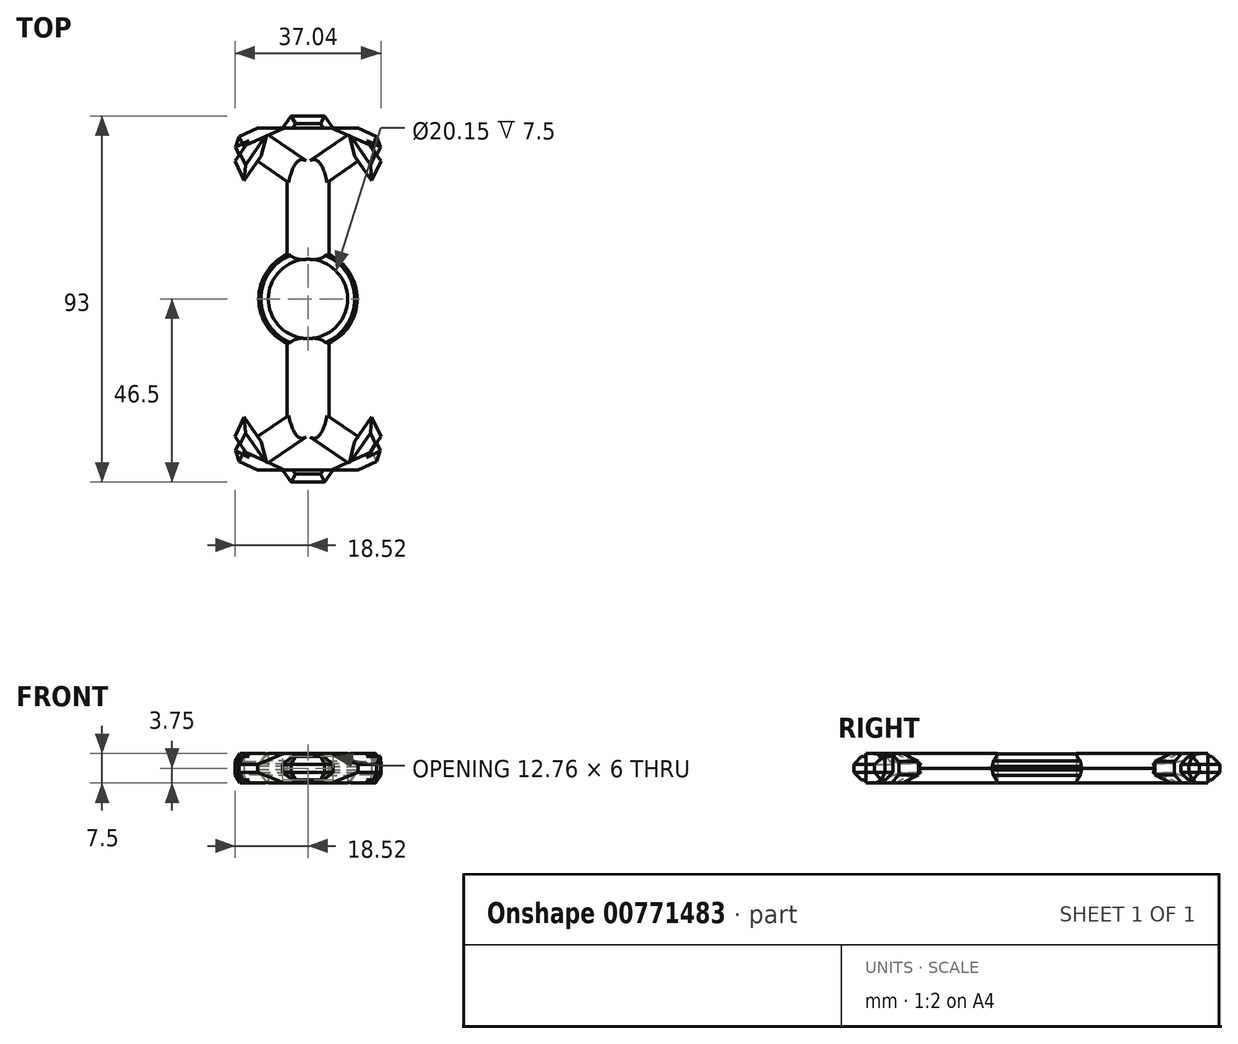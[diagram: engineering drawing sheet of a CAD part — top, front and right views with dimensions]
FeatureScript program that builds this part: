
annotation { "Feature Type Name" : "Feature", "Feature Type Description" : "" }
export const myFeature = defineFeature(function(context is Context, id is Id, definition is map)
    precondition{}
    {
        {
            var Q0;
            Q0=qCreatedBy(makeId("Top.planeOp"),FACE);
            var sketch = newSketch(context, id + "F0", { "sketchPlane" : qUnion([Q0])});
            skCircle(sketch, "E0", {"center": v(0, 0) * mm, "radius": 12.5 * mm});
            skLineSegment(sketch, "E1", {"start": v(0, 0) * mm, "end": v(5.5, 0) * mm});
            skLineSegment(sketch, "E2", {"start": v(5.5, 0) * mm, "end": v(-5.5, 0) * mm});
            skLineSegment(sketch, "E3", {"start": v(-5.5, 0) * mm, "end": v(-5.5, -35) * mm});
            skLineSegment(sketch, "E4", {"start": v(-5.5, -35) * mm, "end": v(5.5, -35) * mm});
            skLineSegment(sketch, "E5", {"start": v(5.5, -35) * mm, "end": v(5.5, 0) * mm});
            skLineSegment(sketch, "E6.MirrorCS", {"start": v(-5.5, 0) * mm, "end": v(-5.5, 35) * mm});
            skLineSegment(sketch, "E7.MirrorCS", {"start": v(-5.5, 35) * mm, "end": v(5.5, 35) * mm});
            skLineSegment(sketch, "E8.MirrorCS", {"start": v(5.5, 35) * mm, "end": v(5.5, 0) * mm});
            skLineSegment(sketch, "E9", {"start": v(5.5, -30.02) * mm, "end": v(12.76, -35) * mm});
            skLineSegment(sketch, "E10", {"start": v(12.76, -35) * mm, "end": v(16.17, -30.02) * mm});
            skLineSegment(sketch, "E11", {"start": v(16.17, -30.02) * mm, "end": v(18.52, -35) * mm});
            skLineSegment(sketch, "E12", {"start": v(18.52, -35) * mm, "end": v(12.76, -43.4) * mm});
            skLineSegment(sketch, "E13", {"start": v(12.76, -43.4) * mm, "end": v(0, -43.4) * mm});
            skLineSegment(sketch, "E14.MirrorCS", {"start": v(-5.5, -30.02) * mm, "end": v(-12.76, -35) * mm});
            skLineSegment(sketch, "E15.MirrorCS", {"start": v(-12.76, -35) * mm, "end": v(-16.17, -30.02) * mm});
            skLineSegment(sketch, "E16.MirrorCS", {"start": v(-16.17, -30.02) * mm, "end": v(-18.52, -35) * mm});
            skLineSegment(sketch, "E17.MirrorCS", {"start": v(-18.52, -35) * mm, "end": v(-12.76, -43.4) * mm});
            skLineSegment(sketch, "E18.MirrorCS", {"start": v(-12.76, -43.4) * mm, "end": v(0, -43.4) * mm});
            skLineSegment(sketch, "E19", {"start": v(-17.43, -36.6) * mm, "end": v(-19.38, -40.43) * mm});
            skLineSegment(sketch, "E20", {"start": v(-19.38, -40.43) * mm, "end": v(-12.76, -43.4) * mm});
            skLineSegment(sketch, "E21.MirrorCS", {"start": v(19.38, -40.43) * mm, "end": v(12.76, -43.4) * mm});
            skLineSegment(sketch, "E22.MirrorCS", {"start": v(17.43, -36.6) * mm, "end": v(19.38, -40.43) * mm});
            skLineSegment(sketch, "E23.MirrorCS", {"start": v(12.76, 43.4) * mm, "end": v(0, 43.4) * mm});
            skLineSegment(sketch, "E24.MirrorCS", {"start": v(-12.76, 43.4) * mm, "end": v(0, 43.4) * mm});
            skLineSegment(sketch, "E25.MirrorCS", {"start": v(-19.38, 40.43) * mm, "end": v(-12.76, 43.4) * mm});
            skLineSegment(sketch, "E26.MirrorCS", {"start": v(-17.43, 36.6) * mm, "end": v(-19.38, 40.43) * mm});
            skLineSegment(sketch, "E27.MirrorCS", {"start": v(-16.17, 30.02) * mm, "end": v(-18.52, 35) * mm});
            skLineSegment(sketch, "E28.MirrorCS", {"start": v(-18.52, 35) * mm, "end": v(-12.76, 43.4) * mm});
            skLineSegment(sketch, "E29.MirrorCS", {"start": v(-12.76, 35) * mm, "end": v(-16.17, 30.02) * mm});
            skLineSegment(sketch, "E30.MirrorCS", {"start": v(-5.5, 30.02) * mm, "end": v(-12.76, 35) * mm});
            skLineSegment(sketch, "E31.MirrorCS", {"start": v(5.5, 30.02) * mm, "end": v(12.76, 35) * mm});
            skLineSegment(sketch, "E32.MirrorCS", {"start": v(12.76, 35) * mm, "end": v(16.17, 30.02) * mm});
            skLineSegment(sketch, "E33.MirrorCS", {"start": v(18.52, 35) * mm, "end": v(12.76, 43.4) * mm});
            skLineSegment(sketch, "E34.MirrorCS", {"start": v(16.17, 30.02) * mm, "end": v(18.52, 35) * mm});
            skLineSegment(sketch, "E35.MirrorCS", {"start": v(19.38, 40.43) * mm, "end": v(12.76, 43.4) * mm});
            skLineSegment(sketch, "E36.MirrorCS", {"start": v(17.43, 36.6) * mm, "end": v(19.38, 40.43) * mm});
            skLineSegment(sketch, "E37", {"start": v(-6.38, -43.4) * mm, "end": v(-4.25, -46.5) * mm});
            skLineSegment(sketch, "E38", {"start": v(-4.25, -46.5) * mm, "end": v(0, -46.5) * mm});
            skLineSegment(sketch, "E39.MirrorCS", {"start": v(4.25, -46.5) * mm, "end": v(0, -46.5) * mm});
            skLineSegment(sketch, "E40.MirrorCS", {"start": v(6.38, -43.4) * mm, "end": v(4.25, -46.5) * mm});
            skLineSegment(sketch, "E41.MirrorCS", {"start": v(-6.38, 43.4) * mm, "end": v(-4.25, 46.5) * mm});
            skLineSegment(sketch, "E42.MirrorCS", {"start": v(4.25, 46.5) * mm, "end": v(0, 46.5) * mm});
            skLineSegment(sketch, "E43.MirrorCS", {"start": v(-4.25, 46.5) * mm, "end": v(0, 46.5) * mm});
            skLineSegment(sketch, "E44.MirrorCS", {"start": v(6.38, 43.4) * mm, "end": v(4.25, 46.5) * mm});
            skCircle(sketch, "E45", {"center": v(0, 0) * mm, "radius": 10.07 * mm});
            skSolve(sketch);
        }
        {
            var Q0;
            {var subQ0=sQuery(id+"F0.wireOp",EDGE,"E6.MirrorCS");var subQ1=sQuery(id+"F0.wireOp",EDGE,"E0");var subQ2=makeQuery(id+"F0.imprint","INTERSECT",VERTEX,{"derivedFrom":[subQ1,subQ0]});Q0=makeQuery(id+"F0.imprint","IMPRINT",FACE,{"disambiguationData":[TD([[makeQuery(id+"F0.imprint","IMPRINT",EDGE,{"disambiguationData":[TD([[subQ2,-1.0]])],"derivedFrom":subQ1}),1.0]])]});}
            var Q1;
            {var subQ0=sQuery(id+"F0.wireOp",EDGE,"E8.MirrorCS");var subQ1=sQuery(id+"F0.wireOp",EDGE,"E0");var subQ2=makeQuery(id+"F0.imprint","INTERSECT",VERTEX,{"derivedFrom":[subQ1,subQ0]});Q1=makeQuery(id+"F0.imprint","IMPRINT",FACE,{"disambiguationData":[TD([[makeQuery(id+"F0.imprint","IMPRINT",EDGE,{"disambiguationData":[TD([[subQ2,1.0]])],"derivedFrom":subQ1}),1.0]])]});}
            var Q2;
            {var subQ0=sQuery(id+"F0.wireOp",EDGE,"E3");var subQ3=sQuery(id+"F0.wireOp",EDGE,"E0");var subQ4=makeQuery(id+"F0.imprint","INTERSECT",VERTEX,{"derivedFrom":[subQ3,subQ0]});Q2=makeQuery(id+"F0.imprint","IMPRINT",FACE,{"disambiguationData":[TD([[makeQuery(id+"F0.imprint","IMPRINT",EDGE,{"disambiguationData":[TD([[subQ4,-1.0]])],"derivedFrom":subQ3}),1.0]])]});}
            var Q3;
            {var subQ0=sQuery(id+"F0.wireOp",EDGE,"E6.MirrorCS");var subQ3=sQuery(id+"F0.wireOp",EDGE,"E0");var subQ4=makeQuery(id+"F0.imprint","INTERSECT",VERTEX,{"derivedFrom":[subQ3,subQ0]});Q3=makeQuery(id+"F0.imprint","IMPRINT",FACE,{"disambiguationData":[TD([[makeQuery(id+"F0.imprint","IMPRINT",EDGE,{"disambiguationData":[TD([[subQ4,1.0]])],"derivedFrom":subQ3}),1.0]])]});}
            var Q4;
            {var subQ9=sQuery(id+"F0.wireOp",EDGE,"E7.MirrorCS");Q4=makeQuery(id+"F0.imprint","IMPRINT",FACE,{"disambiguationData":[TD([[makeQuery(id+"F0.imprint","IMPRINT",EDGE,{"derivedFrom":subQ9}),1.0]])]});}
            var Q5;
            {var subQ8=sQuery(id+"F0.wireOp",EDGE,"E4");Q5=makeQuery(id+"F0.imprint","IMPRINT",FACE,{"disambiguationData":[TD([[makeQuery(id+"F0.imprint","IMPRINT",EDGE,{"derivedFrom":subQ8}),-1.0]])]});}
            var Q6;
            {var subQ0=sQuery(id+"F0.wireOp",EDGE,"E4");Q6=makeQuery(id+"F0.imprint","IMPRINT",FACE,{"disambiguationData":[TD([[makeQuery(id+"F0.imprint","IMPRINT",EDGE,{"derivedFrom":subQ0}),1.0]])]});}
            var Q7;
            {var subQ0=sQuery(id+"F0.wireOp",EDGE,"E7.MirrorCS");Q7=makeQuery(id+"F0.imprint","IMPRINT",FACE,{"disambiguationData":[TD([[makeQuery(id+"F0.imprint","IMPRINT",EDGE,{"derivedFrom":subQ0}),-1.0]])]});}
            extrude(context, id + "F1", {"entities" : qUnion([Q0, Q1, Q2, Q3, Q4, Q5, Q6, Q7]), "endBound" : BoundingType.SYMMETRIC, "depth" : 7.5 * mm, "offsetDistance" : 25 * mm});
        }
        {
            var Q0;
            {var subQ0=sQuery(id+"F0.wireOp",EDGE,"E0");Q0=makeQuery(id+"F1.opExtrude","CAP_EDGE",EDGE,{"disambiguationData":[OSD([subQ0]),TDD([makeQuery(id+"F0.imprint","IMPRINT",EDGE,{"disambiguationData":[TD([[makeQuery(id+"F0.imprint","INTERSECT",VERTEX,{"derivedFrom":[subQ0,sQuery(id+"F0.wireOp",EDGE,"E6.MirrorCS")]}),-1.0]])],"derivedFrom":subQ0})])],"isStart":false});}
            var Q1;
            {var subQ0=sQuery(id+"F0.wireOp",EDGE,"E0");Q1=makeQuery(id+"F1.opExtrude","CAP_EDGE",EDGE,{"disambiguationData":[OSD([subQ0]),TDD([makeQuery(id+"F0.imprint","IMPRINT",EDGE,{"disambiguationData":[TD([[makeQuery(id+"F0.imprint","INTERSECT",VERTEX,{"derivedFrom":[subQ0,sQuery(id+"F0.wireOp",EDGE,"E8.MirrorCS")]}),1.0]])],"derivedFrom":subQ0})])],"isStart":false});}
            var Q2;
            {var subQ0=sQuery(id+"F0.wireOp",EDGE,"E0");Q2=makeQuery(id+"F1.opExtrude","CAP_EDGE",EDGE,{"disambiguationData":[OSD([subQ0]),TDD([makeQuery(id+"F0.imprint","IMPRINT",EDGE,{"disambiguationData":[TD([[makeQuery(id+"F0.imprint","INTERSECT",VERTEX,{"derivedFrom":[subQ0,sQuery(id+"F0.wireOp",EDGE,"E6.MirrorCS")]}),-1.0]])],"derivedFrom":subQ0})])],"isStart":true});}
            var Q3;
            {var subQ0=sQuery(id+"F0.wireOp",EDGE,"E0");Q3=makeQuery(id+"F1.opExtrude","CAP_EDGE",EDGE,{"disambiguationData":[OSD([subQ0]),TDD([makeQuery(id+"F0.imprint","IMPRINT",EDGE,{"disambiguationData":[TD([[makeQuery(id+"F0.imprint","INTERSECT",VERTEX,{"derivedFrom":[subQ0,sQuery(id+"F0.wireOp",EDGE,"E8.MirrorCS")]}),1.0]])],"derivedFrom":subQ0})])],"isStart":true});}
            chamfer(context, id + "F2", {"entities" : qUnion([Q0, Q1, Q2, Q3]), "width" : 2.5 * mm, "tangentPropagation" : true});
        }
        {
            var Q0;
            Q0=makeQuery(id+"F1.opExtrude","CAP_EDGE",EDGE,{"disambiguationData":[OSD([sQuery(id+"F0.wireOp",EDGE,"E5")])],"isStart":false});
            var Q1;
            Q1=makeQuery(id+"F1.opExtrude","CAP_EDGE",EDGE,{"disambiguationData":[OSD([sQuery(id+"F0.wireOp",EDGE,"E3")])],"isStart":false});
            var Q2;
            Q2=makeQuery(id+"F1.opExtrude","CAP_EDGE",EDGE,{"disambiguationData":[OSD([sQuery(id+"F0.wireOp",EDGE,"E3")])],"isStart":true});
            var Q3;
            Q3=makeQuery(id+"F1.opExtrude","CAP_EDGE",EDGE,{"disambiguationData":[OSD([sQuery(id+"F0.wireOp",EDGE,"E5")])],"isStart":true});
            var Q4;
            Q4=makeQuery(id+"F1.opExtrude","CAP_EDGE",EDGE,{"disambiguationData":[OSD([sQuery(id+"F0.wireOp",EDGE,"E6.MirrorCS")])],"isStart":true});
            var Q5;
            Q5=makeQuery(id+"F1.opExtrude","CAP_EDGE",EDGE,{"disambiguationData":[OSD([sQuery(id+"F0.wireOp",EDGE,"E6.MirrorCS")])],"isStart":false});
            var Q6;
            Q6=makeQuery(id+"F1.opExtrude","CAP_EDGE",EDGE,{"disambiguationData":[OSD([sQuery(id+"F0.wireOp",EDGE,"E8.MirrorCS")])],"isStart":true});
            var Q7;
            Q7=makeQuery(id+"F1.opExtrude","CAP_EDGE",EDGE,{"disambiguationData":[OSD([sQuery(id+"F0.wireOp",EDGE,"E8.MirrorCS")])],"isStart":false});
            fillet(context, id + "F3", {"entities" : qUnion([Q0, Q1, Q2, Q3, Q4, Q5, Q6, Q7]), "radius" : 5 * mm, "tangentPropagation" : true, "allowEdgeOverflow" : false});
        }
        {
            var Q0;
            {var subQ3=sQuery(id+"F0.wireOp",EDGE,"E37");Q0=makeQuery(id+"F0.imprint","IMPRINT",FACE,{"disambiguationData":[TD([[makeQuery(id+"F0.imprint","IMPRINT",EDGE,{"derivedFrom":subQ3}),1.0]])]});}
            var Q1;
            {var subQ0=sQuery(id+"F0.wireOp",EDGE,"E21.MirrorCS");Q1=makeQuery(id+"F0.imprint","IMPRINT",FACE,{"disambiguationData":[TD([[makeQuery(id+"F0.imprint","IMPRINT",EDGE,{"derivedFrom":subQ0}),-1.0]])]});}
            var Q2;
            {var subQ2=sQuery(id+"F0.wireOp",EDGE,"E19");Q2=makeQuery(id+"F0.imprint","IMPRINT",FACE,{"disambiguationData":[TD([[makeQuery(id+"F0.imprint","IMPRINT",EDGE,{"derivedFrom":subQ2}),1.0]])]});}
            var Q3;
            {var subQ0=sQuery(id+"F0.wireOp",EDGE,"E25.MirrorCS");Q3=makeQuery(id+"F0.imprint","IMPRINT",FACE,{"disambiguationData":[TD([[makeQuery(id+"F0.imprint","IMPRINT",EDGE,{"derivedFrom":subQ0}),-1.0]])]});}
            var Q4;
            {var subQ0=sQuery(id+"F0.wireOp",EDGE,"E41.MirrorCS");Q4=makeQuery(id+"F0.imprint","IMPRINT",FACE,{"disambiguationData":[TD([[makeQuery(id+"F0.imprint","IMPRINT",EDGE,{"derivedFrom":subQ0}),-1.0]])]});}
            var Q5;
            {var subQ0=sQuery(id+"F0.wireOp",EDGE,"E35.MirrorCS");Q5=makeQuery(id+"F0.imprint","IMPRINT",FACE,{"disambiguationData":[TD([[makeQuery(id+"F0.imprint","IMPRINT",EDGE,{"derivedFrom":subQ0}),1.0]])]});}
            extrude(context, id + "F4", {"entities" : qUnion([Q0, Q1, Q2, Q3, Q4, Q5]), "operationType" : NewBodyOperationType.ADD, "endBound" : BoundingType.SYMMETRIC, "depth" : 6 * mm, "offsetDistance" : 25 * mm});
        }
        {
            var Q0;
            Q0=makeQuery(id+"F4.opExtrude","CAP_EDGE",EDGE,{"disambiguationData":[OSD([sQuery(id+"F0.wireOp",EDGE,"E42.MirrorCS"),sQuery(id+"F0.wireOp",EDGE,"E43.MirrorCS")])],"isStart":false});
            var Q1;
            Q1=makeQuery(id+"F4.opExtrude","CAP_EDGE",EDGE,{"disambiguationData":[OSD([sQuery(id+"F0.wireOp",EDGE,"E42.MirrorCS"),sQuery(id+"F0.wireOp",EDGE,"E43.MirrorCS")])],"isStart":true});
            var Q2;
            Q2=makeQuery(id+"F4.opExtrude","CAP_EDGE",EDGE,{"disambiguationData":[OSD([sQuery(id+"F0.wireOp",EDGE,"E41.MirrorCS")])],"isStart":false});
            var Q3;
            Q3=makeQuery(id+"F4.opExtrude","CAP_EDGE",EDGE,{"disambiguationData":[OSD([sQuery(id+"F0.wireOp",EDGE,"E41.MirrorCS")])],"isStart":true});
            var Q4;
            Q4=makeQuery(id+"F4.opExtrude","CAP_EDGE",EDGE,{"disambiguationData":[OSD([sQuery(id+"F0.wireOp",EDGE,"E44.MirrorCS")])],"isStart":false});
            var Q5;
            Q5=makeQuery(id+"F4.opExtrude","CAP_EDGE",EDGE,{"disambiguationData":[OSD([sQuery(id+"F0.wireOp",EDGE,"E44.MirrorCS")])],"isStart":true});
            var Q6;
            Q6=makeQuery(id+"F4.opExtrude","CAP_EDGE",EDGE,{"disambiguationData":[OSD([sQuery(id+"F0.wireOp",EDGE,"E35.MirrorCS")])],"isStart":false});
            var Q7;
            Q7=makeQuery(id+"F4.opExtrude","CAP_EDGE",EDGE,{"disambiguationData":[OSD([sQuery(id+"F0.wireOp",EDGE,"E36.MirrorCS")])],"isStart":false});
            var Q8;
            Q8=makeQuery(id+"F4.opExtrude","CAP_EDGE",EDGE,{"disambiguationData":[OSD([sQuery(id+"F0.wireOp",EDGE,"E35.MirrorCS")])],"isStart":true});
            var Q9;
            Q9=makeQuery(id+"F4.opExtrude","CAP_EDGE",EDGE,{"disambiguationData":[OSD([sQuery(id+"F0.wireOp",EDGE,"E36.MirrorCS")])],"isStart":true});
            var Q10;
            Q10=makeQuery(id+"F4.opExtrude","CAP_EDGE",EDGE,{"disambiguationData":[OSD([sQuery(id+"F0.wireOp",EDGE,"E25.MirrorCS")])],"isStart":false});
            var Q11;
            Q11=makeQuery(id+"F4.opExtrude","CAP_EDGE",EDGE,{"disambiguationData":[OSD([sQuery(id+"F0.wireOp",EDGE,"E25.MirrorCS")])],"isStart":true});
            var Q12;
            Q12=makeQuery(id+"F4.opExtrude","SWEPT_EDGE",EDGE,{"disambiguationData":[OSD([sQuery(id+"F0.wireOp",EDGE,"E25.MirrorCS"),sQuery(id+"F0.wireOp",EDGE,"E26.MirrorCS")])]});
            var Q13;
            Q13=makeQuery(id+"F4.opExtrude","CAP_EDGE",EDGE,{"disambiguationData":[OSD([sQuery(id+"F0.wireOp",EDGE,"E26.MirrorCS")])],"isStart":false});
            var Q14;
            Q14=makeQuery(id+"F4.opExtrude","CAP_EDGE",EDGE,{"disambiguationData":[OSD([sQuery(id+"F0.wireOp",EDGE,"E26.MirrorCS")])],"isStart":true});
            var Q15;
            Q15=makeQuery(id+"F4.opExtrude","SWEPT_EDGE",EDGE,{"disambiguationData":[OSD([sQuery(id+"F0.wireOp",EDGE,"E35.MirrorCS"),sQuery(id+"F0.wireOp",EDGE,"E36.MirrorCS")])]});
            var Q16;
            Q16=makeQuery(id+"F1.opExtrude","CAP_EDGE",EDGE,{"disambiguationData":[OSD([sQuery(id+"F0.wireOp",EDGE,"E34.MirrorCS")])],"isStart":false});
            var Q17;
            Q17=makeQuery(id+"F1.opExtrude","CAP_EDGE",EDGE,{"disambiguationData":[OSD([sQuery(id+"F0.wireOp",EDGE,"E34.MirrorCS")])],"isStart":true});
            var Q18;
            Q18=makeQuery(id+"F1.opExtrude","CAP_EDGE",EDGE,{"disambiguationData":[OSD([sQuery(id+"F0.wireOp",EDGE,"E27.MirrorCS")])],"isStart":false});
            var Q19;
            Q19=makeQuery(id+"F1.opExtrude","CAP_EDGE",EDGE,{"disambiguationData":[OSD([sQuery(id+"F0.wireOp",EDGE,"E27.MirrorCS")])],"isStart":true});
            var Q20;
            Q20=makeQuery(id+"F4.opExtrude","CAP_EDGE",EDGE,{"disambiguationData":[OSD([sQuery(id+"F0.wireOp",EDGE,"E38"),sQuery(id+"F0.wireOp",EDGE,"E39.MirrorCS")])],"isStart":true});
            var Q21;
            Q21=makeQuery(id+"F4.opExtrude","CAP_EDGE",EDGE,{"disambiguationData":[OSD([sQuery(id+"F0.wireOp",EDGE,"E38"),sQuery(id+"F0.wireOp",EDGE,"E39.MirrorCS")])],"isStart":false});
            var Q22;
            Q22=makeQuery(id+"F4.opExtrude","CAP_EDGE",EDGE,{"disambiguationData":[OSD([sQuery(id+"F0.wireOp",EDGE,"E40.MirrorCS")])],"isStart":false});
            var Q23;
            Q23=makeQuery(id+"F4.opExtrude","CAP_EDGE",EDGE,{"disambiguationData":[OSD([sQuery(id+"F0.wireOp",EDGE,"E40.MirrorCS")])],"isStart":true});
            var Q24;
            Q24=makeQuery(id+"F4.opExtrude","CAP_EDGE",EDGE,{"disambiguationData":[OSD([sQuery(id+"F0.wireOp",EDGE,"E37")])],"isStart":false});
            var Q25;
            Q25=makeQuery(id+"F4.opExtrude","CAP_EDGE",EDGE,{"disambiguationData":[OSD([sQuery(id+"F0.wireOp",EDGE,"E37")])],"isStart":true});
            var Q26;
            Q26=makeQuery(id+"F4.opExtrude","CAP_EDGE",EDGE,{"disambiguationData":[OSD([sQuery(id+"F0.wireOp",EDGE,"E20")])],"isStart":false});
            var Q27;
            Q27=makeQuery(id+"F4.opExtrude","CAP_EDGE",EDGE,{"disambiguationData":[OSD([sQuery(id+"F0.wireOp",EDGE,"E20")])],"isStart":true});
            var Q28;
            Q28=makeQuery(id+"F4.opExtrude","SWEPT_EDGE",EDGE,{"disambiguationData":[OSD([sQuery(id+"F0.wireOp",EDGE,"E19"),sQuery(id+"F0.wireOp",EDGE,"E20")])]});
            var Q29;
            Q29=makeQuery(id+"F4.opExtrude","CAP_EDGE",EDGE,{"disambiguationData":[OSD([sQuery(id+"F0.wireOp",EDGE,"E19")])],"isStart":true});
            var Q30;
            Q30=makeQuery(id+"F4.opExtrude","CAP_EDGE",EDGE,{"disambiguationData":[OSD([sQuery(id+"F0.wireOp",EDGE,"E19")])],"isStart":false});
            var Q31;
            Q31=makeQuery(id+"F1.opExtrude","CAP_EDGE",EDGE,{"disambiguationData":[OSD([sQuery(id+"F0.wireOp",EDGE,"E16.MirrorCS")])],"isStart":true});
            var Q32;
            Q32=makeQuery(id+"F1.opExtrude","CAP_EDGE",EDGE,{"disambiguationData":[OSD([sQuery(id+"F0.wireOp",EDGE,"E16.MirrorCS")])],"isStart":false});
            var Q33;
            Q33=makeQuery(id+"F1.opExtrude","CAP_EDGE",EDGE,{"disambiguationData":[OSD([sQuery(id+"F0.wireOp",EDGE,"E11")])],"isStart":true});
            var Q34;
            Q34=makeQuery(id+"F1.opExtrude","CAP_EDGE",EDGE,{"disambiguationData":[OSD([sQuery(id+"F0.wireOp",EDGE,"E11")])],"isStart":false});
            var Q35;
            Q35=makeQuery(id+"F4.opExtrude","CAP_EDGE",EDGE,{"disambiguationData":[OSD([sQuery(id+"F0.wireOp",EDGE,"E22.MirrorCS")])],"isStart":true});
            var Q36;
            Q36=makeQuery(id+"F4.opExtrude","CAP_EDGE",EDGE,{"disambiguationData":[OSD([sQuery(id+"F0.wireOp",EDGE,"E21.MirrorCS")])],"isStart":true});
            var Q37;
            Q37=makeQuery(id+"F4.opExtrude","CAP_EDGE",EDGE,{"disambiguationData":[OSD([sQuery(id+"F0.wireOp",EDGE,"E21.MirrorCS")])],"isStart":false});
            var Q38;
            Q38=makeQuery(id+"F4.opExtrude","SWEPT_EDGE",EDGE,{"disambiguationData":[OSD([sQuery(id+"F0.wireOp",EDGE,"E21.MirrorCS"),sQuery(id+"F0.wireOp",EDGE,"E22.MirrorCS")])]});
            var Q39;
            {var subQ0=sQuery(id+"F0.wireOp",EDGE,"E0");var subQ1=makeQuery(id+"F0.imprint","IMPRINT",EDGE,{"disambiguationData":[TD([[makeQuery(id+"F0.imprint","INTERSECT",VERTEX,{"derivedFrom":[subQ0,sQuery(id+"F0.wireOp",EDGE,"E6.MirrorCS")]}),-1.0]])],"derivedFrom":subQ0});Q39=makeQuery(id+"F2.opChamfer","BLEND_EDGE",EDGE,{"blendedFrom":[makeQuery(id+"F1.opExtrude","CAP_EDGE",EDGE,{"disambiguationData":[OSD([subQ0]),TDD([subQ1])],"isStart":true}),makeQuery(id+"F1.opExtrude","SWEPT_FACE",FACE,{"disambiguationData":[OSD([subQ0]),TDD([subQ1])]})],"blendedInto":[makeQuery(id+"F1.opExtrude","SWEPT_FACE",FACE,{"disambiguationData":[OSD([subQ0]),TDD([subQ1])]})]});}
            var Q40;
            {var subQ0=sQuery(id+"F0.wireOp",EDGE,"E0");var subQ1=makeQuery(id+"F0.imprint","IMPRINT",EDGE,{"disambiguationData":[TD([[makeQuery(id+"F0.imprint","INTERSECT",VERTEX,{"derivedFrom":[subQ0,sQuery(id+"F0.wireOp",EDGE,"E6.MirrorCS")]}),-1.0]])],"derivedFrom":subQ0});Q40=makeQuery(id+"F2.opChamfer","BLEND_EDGE",EDGE,{"blendedFrom":[makeQuery(id+"F1.opExtrude","CAP_EDGE",EDGE,{"disambiguationData":[OSD([subQ0]),TDD([subQ1])],"isStart":false}),makeQuery(id+"F1.opExtrude","SWEPT_FACE",FACE,{"disambiguationData":[OSD([subQ0]),TDD([subQ1])]})],"blendedInto":[makeQuery(id+"F1.opExtrude","SWEPT_FACE",FACE,{"disambiguationData":[OSD([subQ0]),TDD([subQ1])]})]});}
            var Q41;
            {var subQ0=sQuery(id+"F0.wireOp",EDGE,"E0");var subQ1=makeQuery(id+"F0.imprint","IMPRINT",EDGE,{"disambiguationData":[TD([[makeQuery(id+"F0.imprint","INTERSECT",VERTEX,{"derivedFrom":[subQ0,sQuery(id+"F0.wireOp",EDGE,"E8.MirrorCS")]}),1.0]])],"derivedFrom":subQ0});Q41=makeQuery(id+"F2.opChamfer","BLEND_EDGE",EDGE,{"blendedFrom":[makeQuery(id+"F1.opExtrude","CAP_EDGE",EDGE,{"disambiguationData":[OSD([subQ0]),TDD([subQ1])],"isStart":true}),makeQuery(id+"F1.opExtrude","SWEPT_FACE",FACE,{"disambiguationData":[OSD([subQ0]),TDD([subQ1])]})],"blendedInto":[makeQuery(id+"F1.opExtrude","SWEPT_FACE",FACE,{"disambiguationData":[OSD([subQ0]),TDD([subQ1])]})]});}
            var Q42;
            {var subQ0=sQuery(id+"F0.wireOp",EDGE,"E0");var subQ1=makeQuery(id+"F0.imprint","IMPRINT",EDGE,{"disambiguationData":[TD([[makeQuery(id+"F0.imprint","INTERSECT",VERTEX,{"derivedFrom":[subQ0,sQuery(id+"F0.wireOp",EDGE,"E8.MirrorCS")]}),1.0]])],"derivedFrom":subQ0});Q42=makeQuery(id+"F2.opChamfer","BLEND_EDGE",EDGE,{"blendedFrom":[makeQuery(id+"F1.opExtrude","CAP_EDGE",EDGE,{"disambiguationData":[OSD([subQ0]),TDD([subQ1])],"isStart":false}),makeQuery(id+"F1.opExtrude","SWEPT_FACE",FACE,{"disambiguationData":[OSD([subQ0]),TDD([subQ1])]})],"blendedInto":[makeQuery(id+"F1.opExtrude","SWEPT_FACE",FACE,{"disambiguationData":[OSD([subQ0]),TDD([subQ1])]})]});}
            var Q43;
            {var subQ0=sQuery(id+"F0.wireOp",EDGE,"E8.MirrorCS");var subQ1=sQuery(id+"F0.wireOp",EDGE,"E5");var subQ2=sQuery(id+"F0.wireOp",EDGE,"E0");Q43=makeQuery(id+"F2.opChamfer","BLEND_EDGE",EDGE,{"blendedFrom":[makeQuery(id+"F1.opExtrude","CAP_EDGE",EDGE,{"disambiguationData":[OSD([subQ2]),TDD([makeQuery(id+"F0.imprint","IMPRINT",EDGE,{"disambiguationData":[TD([[makeQuery(id+"F0.imprint","INTERSECT",VERTEX,{"derivedFrom":[subQ2,subQ0]}),1.0]])],"derivedFrom":subQ2})])],"isStart":true}),makeQuery(id+"F1.opExtrude","CAP_FACE",FACE,{"disambiguationData":[OSD([subQ2,sQuery(id+"F0.wireOp",EDGE,"E3"),subQ1,sQuery(id+"F0.wireOp",EDGE,"E6.MirrorCS"),subQ0,sQuery(id+"F0.wireOp",EDGE,"E9"),sQuery(id+"F0.wireOp",EDGE,"E10"),sQuery(id+"F0.wireOp",EDGE,"E11"),sQuery(id+"F0.wireOp",EDGE,"E12"),sQuery(id+"F0.wireOp",EDGE,"E13"),sQuery(id+"F0.wireOp",EDGE,"E14.MirrorCS"),sQuery(id+"F0.wireOp",EDGE,"E15.MirrorCS"),sQuery(id+"F0.wireOp",EDGE,"E16.MirrorCS"),sQuery(id+"F0.wireOp",EDGE,"E17.MirrorCS"),sQuery(id+"F0.wireOp",EDGE,"E18.MirrorCS"),sQuery(id+"F0.wireOp",EDGE,"E23.MirrorCS"),sQuery(id+"F0.wireOp",EDGE,"E24.MirrorCS"),sQuery(id+"F0.wireOp",EDGE,"E27.MirrorCS"),sQuery(id+"F0.wireOp",EDGE,"E28.MirrorCS"),sQuery(id+"F0.wireOp",EDGE,"E29.MirrorCS"),sQuery(id+"F0.wireOp",EDGE,"E30.MirrorCS"),sQuery(id+"F0.wireOp",EDGE,"E31.MirrorCS"),sQuery(id+"F0.wireOp",EDGE,"E32.MirrorCS"),sQuery(id+"F0.wireOp",EDGE,"E33.MirrorCS"),sQuery(id+"F0.wireOp",EDGE,"E34.MirrorCS")])],"isStart":true})],"blendedInto":[makeQuery(id+"F1.opExtrude","CAP_FACE",FACE,{"disambiguationData":[OSD([subQ2,sQuery(id+"F0.wireOp",EDGE,"E3"),subQ1,sQuery(id+"F0.wireOp",EDGE,"E6.MirrorCS"),subQ0,sQuery(id+"F0.wireOp",EDGE,"E9"),sQuery(id+"F0.wireOp",EDGE,"E10"),sQuery(id+"F0.wireOp",EDGE,"E11"),sQuery(id+"F0.wireOp",EDGE,"E12"),sQuery(id+"F0.wireOp",EDGE,"E13"),sQuery(id+"F0.wireOp",EDGE,"E14.MirrorCS"),sQuery(id+"F0.wireOp",EDGE,"E15.MirrorCS"),sQuery(id+"F0.wireOp",EDGE,"E16.MirrorCS"),sQuery(id+"F0.wireOp",EDGE,"E17.MirrorCS"),sQuery(id+"F0.wireOp",EDGE,"E18.MirrorCS"),sQuery(id+"F0.wireOp",EDGE,"E23.MirrorCS"),sQuery(id+"F0.wireOp",EDGE,"E24.MirrorCS"),sQuery(id+"F0.wireOp",EDGE,"E27.MirrorCS"),sQuery(id+"F0.wireOp",EDGE,"E28.MirrorCS"),sQuery(id+"F0.wireOp",EDGE,"E29.MirrorCS"),sQuery(id+"F0.wireOp",EDGE,"E30.MirrorCS"),sQuery(id+"F0.wireOp",EDGE,"E31.MirrorCS"),sQuery(id+"F0.wireOp",EDGE,"E32.MirrorCS"),sQuery(id+"F0.wireOp",EDGE,"E33.MirrorCS"),sQuery(id+"F0.wireOp",EDGE,"E34.MirrorCS")])],"isStart":true})]});}
            var Q44;
            {var subQ0=sQuery(id+"F0.wireOp",EDGE,"E6.MirrorCS");var subQ1=sQuery(id+"F0.wireOp",EDGE,"E3");var subQ2=sQuery(id+"F0.wireOp",EDGE,"E0");Q44=makeQuery(id+"F2.opChamfer","BLEND_EDGE",EDGE,{"blendedFrom":[makeQuery(id+"F1.opExtrude","CAP_EDGE",EDGE,{"disambiguationData":[OSD([subQ2]),TDD([makeQuery(id+"F0.imprint","IMPRINT",EDGE,{"disambiguationData":[TD([[makeQuery(id+"F0.imprint","INTERSECT",VERTEX,{"derivedFrom":[subQ2,subQ0]}),-1.0]])],"derivedFrom":subQ2})])],"isStart":true}),makeQuery(id+"F1.opExtrude","CAP_FACE",FACE,{"disambiguationData":[OSD([subQ2,subQ1,sQuery(id+"F0.wireOp",EDGE,"E5"),subQ0,sQuery(id+"F0.wireOp",EDGE,"E8.MirrorCS"),sQuery(id+"F0.wireOp",EDGE,"E9"),sQuery(id+"F0.wireOp",EDGE,"E10"),sQuery(id+"F0.wireOp",EDGE,"E11"),sQuery(id+"F0.wireOp",EDGE,"E12"),sQuery(id+"F0.wireOp",EDGE,"E13"),sQuery(id+"F0.wireOp",EDGE,"E14.MirrorCS"),sQuery(id+"F0.wireOp",EDGE,"E15.MirrorCS"),sQuery(id+"F0.wireOp",EDGE,"E16.MirrorCS"),sQuery(id+"F0.wireOp",EDGE,"E17.MirrorCS"),sQuery(id+"F0.wireOp",EDGE,"E18.MirrorCS"),sQuery(id+"F0.wireOp",EDGE,"E23.MirrorCS"),sQuery(id+"F0.wireOp",EDGE,"E24.MirrorCS"),sQuery(id+"F0.wireOp",EDGE,"E27.MirrorCS"),sQuery(id+"F0.wireOp",EDGE,"E28.MirrorCS"),sQuery(id+"F0.wireOp",EDGE,"E29.MirrorCS"),sQuery(id+"F0.wireOp",EDGE,"E30.MirrorCS"),sQuery(id+"F0.wireOp",EDGE,"E31.MirrorCS"),sQuery(id+"F0.wireOp",EDGE,"E32.MirrorCS"),sQuery(id+"F0.wireOp",EDGE,"E33.MirrorCS"),sQuery(id+"F0.wireOp",EDGE,"E34.MirrorCS")])],"isStart":true})],"blendedInto":[makeQuery(id+"F1.opExtrude","CAP_FACE",FACE,{"disambiguationData":[OSD([subQ2,subQ1,sQuery(id+"F0.wireOp",EDGE,"E5"),subQ0,sQuery(id+"F0.wireOp",EDGE,"E8.MirrorCS"),sQuery(id+"F0.wireOp",EDGE,"E9"),sQuery(id+"F0.wireOp",EDGE,"E10"),sQuery(id+"F0.wireOp",EDGE,"E11"),sQuery(id+"F0.wireOp",EDGE,"E12"),sQuery(id+"F0.wireOp",EDGE,"E13"),sQuery(id+"F0.wireOp",EDGE,"E14.MirrorCS"),sQuery(id+"F0.wireOp",EDGE,"E15.MirrorCS"),sQuery(id+"F0.wireOp",EDGE,"E16.MirrorCS"),sQuery(id+"F0.wireOp",EDGE,"E17.MirrorCS"),sQuery(id+"F0.wireOp",EDGE,"E18.MirrorCS"),sQuery(id+"F0.wireOp",EDGE,"E23.MirrorCS"),sQuery(id+"F0.wireOp",EDGE,"E24.MirrorCS"),sQuery(id+"F0.wireOp",EDGE,"E27.MirrorCS"),sQuery(id+"F0.wireOp",EDGE,"E28.MirrorCS"),sQuery(id+"F0.wireOp",EDGE,"E29.MirrorCS"),sQuery(id+"F0.wireOp",EDGE,"E30.MirrorCS"),sQuery(id+"F0.wireOp",EDGE,"E31.MirrorCS"),sQuery(id+"F0.wireOp",EDGE,"E32.MirrorCS"),sQuery(id+"F0.wireOp",EDGE,"E33.MirrorCS"),sQuery(id+"F0.wireOp",EDGE,"E34.MirrorCS")])],"isStart":true})]});}
            var Q45;
            {var subQ0=sQuery(id+"F0.wireOp",EDGE,"E8.MirrorCS");var subQ1=sQuery(id+"F0.wireOp",EDGE,"E5");var subQ2=sQuery(id+"F0.wireOp",EDGE,"E0");Q45=makeQuery(id+"F2.opChamfer","BLEND_EDGE",EDGE,{"blendedFrom":[makeQuery(id+"F1.opExtrude","CAP_EDGE",EDGE,{"disambiguationData":[OSD([subQ2]),TDD([makeQuery(id+"F0.imprint","IMPRINT",EDGE,{"disambiguationData":[TD([[makeQuery(id+"F0.imprint","INTERSECT",VERTEX,{"derivedFrom":[subQ2,subQ0]}),1.0]])],"derivedFrom":subQ2})])],"isStart":false}),makeQuery(id+"F1.opExtrude","CAP_FACE",FACE,{"disambiguationData":[OSD([subQ2,sQuery(id+"F0.wireOp",EDGE,"E3"),subQ1,sQuery(id+"F0.wireOp",EDGE,"E6.MirrorCS"),subQ0,sQuery(id+"F0.wireOp",EDGE,"E9"),sQuery(id+"F0.wireOp",EDGE,"E10"),sQuery(id+"F0.wireOp",EDGE,"E11"),sQuery(id+"F0.wireOp",EDGE,"E12"),sQuery(id+"F0.wireOp",EDGE,"E13"),sQuery(id+"F0.wireOp",EDGE,"E14.MirrorCS"),sQuery(id+"F0.wireOp",EDGE,"E15.MirrorCS"),sQuery(id+"F0.wireOp",EDGE,"E16.MirrorCS"),sQuery(id+"F0.wireOp",EDGE,"E17.MirrorCS"),sQuery(id+"F0.wireOp",EDGE,"E18.MirrorCS"),sQuery(id+"F0.wireOp",EDGE,"E23.MirrorCS"),sQuery(id+"F0.wireOp",EDGE,"E24.MirrorCS"),sQuery(id+"F0.wireOp",EDGE,"E27.MirrorCS"),sQuery(id+"F0.wireOp",EDGE,"E28.MirrorCS"),sQuery(id+"F0.wireOp",EDGE,"E29.MirrorCS"),sQuery(id+"F0.wireOp",EDGE,"E30.MirrorCS"),sQuery(id+"F0.wireOp",EDGE,"E31.MirrorCS"),sQuery(id+"F0.wireOp",EDGE,"E32.MirrorCS"),sQuery(id+"F0.wireOp",EDGE,"E33.MirrorCS"),sQuery(id+"F0.wireOp",EDGE,"E34.MirrorCS")])],"isStart":false})],"blendedInto":[makeQuery(id+"F1.opExtrude","CAP_FACE",FACE,{"disambiguationData":[OSD([subQ2,sQuery(id+"F0.wireOp",EDGE,"E3"),subQ1,sQuery(id+"F0.wireOp",EDGE,"E6.MirrorCS"),subQ0,sQuery(id+"F0.wireOp",EDGE,"E9"),sQuery(id+"F0.wireOp",EDGE,"E10"),sQuery(id+"F0.wireOp",EDGE,"E11"),sQuery(id+"F0.wireOp",EDGE,"E12"),sQuery(id+"F0.wireOp",EDGE,"E13"),sQuery(id+"F0.wireOp",EDGE,"E14.MirrorCS"),sQuery(id+"F0.wireOp",EDGE,"E15.MirrorCS"),sQuery(id+"F0.wireOp",EDGE,"E16.MirrorCS"),sQuery(id+"F0.wireOp",EDGE,"E17.MirrorCS"),sQuery(id+"F0.wireOp",EDGE,"E18.MirrorCS"),sQuery(id+"F0.wireOp",EDGE,"E23.MirrorCS"),sQuery(id+"F0.wireOp",EDGE,"E24.MirrorCS"),sQuery(id+"F0.wireOp",EDGE,"E27.MirrorCS"),sQuery(id+"F0.wireOp",EDGE,"E28.MirrorCS"),sQuery(id+"F0.wireOp",EDGE,"E29.MirrorCS"),sQuery(id+"F0.wireOp",EDGE,"E30.MirrorCS"),sQuery(id+"F0.wireOp",EDGE,"E31.MirrorCS"),sQuery(id+"F0.wireOp",EDGE,"E32.MirrorCS"),sQuery(id+"F0.wireOp",EDGE,"E33.MirrorCS"),sQuery(id+"F0.wireOp",EDGE,"E34.MirrorCS")])],"isStart":false})]});}
            var Q46;
            {var subQ0=sQuery(id+"F0.wireOp",EDGE,"E6.MirrorCS");var subQ1=sQuery(id+"F0.wireOp",EDGE,"E3");var subQ2=sQuery(id+"F0.wireOp",EDGE,"E0");Q46=makeQuery(id+"F2.opChamfer","BLEND_EDGE",EDGE,{"blendedFrom":[makeQuery(id+"F1.opExtrude","CAP_EDGE",EDGE,{"disambiguationData":[OSD([subQ2]),TDD([makeQuery(id+"F0.imprint","IMPRINT",EDGE,{"disambiguationData":[TD([[makeQuery(id+"F0.imprint","INTERSECT",VERTEX,{"derivedFrom":[subQ2,subQ0]}),-1.0]])],"derivedFrom":subQ2})])],"isStart":false}),makeQuery(id+"F1.opExtrude","CAP_FACE",FACE,{"disambiguationData":[OSD([subQ2,subQ1,sQuery(id+"F0.wireOp",EDGE,"E5"),subQ0,sQuery(id+"F0.wireOp",EDGE,"E8.MirrorCS"),sQuery(id+"F0.wireOp",EDGE,"E9"),sQuery(id+"F0.wireOp",EDGE,"E10"),sQuery(id+"F0.wireOp",EDGE,"E11"),sQuery(id+"F0.wireOp",EDGE,"E12"),sQuery(id+"F0.wireOp",EDGE,"E13"),sQuery(id+"F0.wireOp",EDGE,"E14.MirrorCS"),sQuery(id+"F0.wireOp",EDGE,"E15.MirrorCS"),sQuery(id+"F0.wireOp",EDGE,"E16.MirrorCS"),sQuery(id+"F0.wireOp",EDGE,"E17.MirrorCS"),sQuery(id+"F0.wireOp",EDGE,"E18.MirrorCS"),sQuery(id+"F0.wireOp",EDGE,"E23.MirrorCS"),sQuery(id+"F0.wireOp",EDGE,"E24.MirrorCS"),sQuery(id+"F0.wireOp",EDGE,"E27.MirrorCS"),sQuery(id+"F0.wireOp",EDGE,"E28.MirrorCS"),sQuery(id+"F0.wireOp",EDGE,"E29.MirrorCS"),sQuery(id+"F0.wireOp",EDGE,"E30.MirrorCS"),sQuery(id+"F0.wireOp",EDGE,"E31.MirrorCS"),sQuery(id+"F0.wireOp",EDGE,"E32.MirrorCS"),sQuery(id+"F0.wireOp",EDGE,"E33.MirrorCS"),sQuery(id+"F0.wireOp",EDGE,"E34.MirrorCS")])],"isStart":false})],"blendedInto":[makeQuery(id+"F1.opExtrude","CAP_FACE",FACE,{"disambiguationData":[OSD([subQ2,subQ1,sQuery(id+"F0.wireOp",EDGE,"E5"),subQ0,sQuery(id+"F0.wireOp",EDGE,"E8.MirrorCS"),sQuery(id+"F0.wireOp",EDGE,"E9"),sQuery(id+"F0.wireOp",EDGE,"E10"),sQuery(id+"F0.wireOp",EDGE,"E11"),sQuery(id+"F0.wireOp",EDGE,"E12"),sQuery(id+"F0.wireOp",EDGE,"E13"),sQuery(id+"F0.wireOp",EDGE,"E14.MirrorCS"),sQuery(id+"F0.wireOp",EDGE,"E15.MirrorCS"),sQuery(id+"F0.wireOp",EDGE,"E16.MirrorCS"),sQuery(id+"F0.wireOp",EDGE,"E17.MirrorCS"),sQuery(id+"F0.wireOp",EDGE,"E18.MirrorCS"),sQuery(id+"F0.wireOp",EDGE,"E23.MirrorCS"),sQuery(id+"F0.wireOp",EDGE,"E24.MirrorCS"),sQuery(id+"F0.wireOp",EDGE,"E27.MirrorCS"),sQuery(id+"F0.wireOp",EDGE,"E28.MirrorCS"),sQuery(id+"F0.wireOp",EDGE,"E29.MirrorCS"),sQuery(id+"F0.wireOp",EDGE,"E30.MirrorCS"),sQuery(id+"F0.wireOp",EDGE,"E31.MirrorCS"),sQuery(id+"F0.wireOp",EDGE,"E32.MirrorCS"),sQuery(id+"F0.wireOp",EDGE,"E33.MirrorCS"),sQuery(id+"F0.wireOp",EDGE,"E34.MirrorCS")])],"isStart":false})]});}
            chamfer(context, id + "F5", {"entities" : qUnion([Q0, Q1, Q2, Q3, Q4, Q5, Q6, Q7, Q8, Q9, Q10, Q11, Q12, Q13, Q14, Q15, Q16, Q17, Q18, Q19, Q20, Q21, Q22, Q23, Q24, Q25, Q26, Q27, Q28, Q29, Q30, Q31, Q32, Q33, Q34, Q35, Q36, Q37, Q38, Q39, Q40, Q41, Q42, Q43, Q44, Q45, Q46]), "width" : 2 * mm, "tangentPropagation" : true});
        }
        {
            var Q0;
            Q0=makeQuery(id+"F1.opExtrude","CAP_EDGE",EDGE,{"disambiguationData":[OSD([sQuery(id+"F0.wireOp",EDGE,"E14.MirrorCS")])],"isStart":false});
            var Q1;
            Q1=makeQuery(id+"F1.opExtrude","CAP_EDGE",EDGE,{"disambiguationData":[OSD([sQuery(id+"F0.wireOp",EDGE,"E9")])],"isStart":false});
            var Q2;
            Q2=makeQuery(id+"F1.opExtrude","CAP_EDGE",EDGE,{"disambiguationData":[OSD([sQuery(id+"F0.wireOp",EDGE,"E9")])],"isStart":true});
            var Q3;
            Q3=makeQuery(id+"F1.opExtrude","CAP_EDGE",EDGE,{"disambiguationData":[OSD([sQuery(id+"F0.wireOp",EDGE,"E14.MirrorCS")])],"isStart":true});
            var Q4;
            Q4=makeQuery(id+"F1.opExtrude","CAP_EDGE",EDGE,{"disambiguationData":[OSD([sQuery(id+"F0.wireOp",EDGE,"E30.MirrorCS")])],"isStart":true});
            var Q5;
            Q5=makeQuery(id+"F1.opExtrude","CAP_EDGE",EDGE,{"disambiguationData":[OSD([sQuery(id+"F0.wireOp",EDGE,"E31.MirrorCS")])],"isStart":false});
            chamfer(context, id + "F6", {"entities" : qUnion([Q0, Q1, Q2, Q3, Q4, Q5]), "chamferType" : ChamferType.OFFSET_ANGLE, "width" : 7 * mm, "oppositeDirection" : false, "angle" : 20 * degree, "tangentPropagation" : true});
        }
        {
            var Q0;
            Q0=makeQuery(id+"F1.opExtrude","CAP_EDGE",EDGE,{"disambiguationData":[OSD([sQuery(id+"F0.wireOp",EDGE,"E31.MirrorCS")])],"isStart":true});
            var Q1;
            Q1=makeQuery(id+"F1.opExtrude","CAP_EDGE",EDGE,{"disambiguationData":[OSD([sQuery(id+"F0.wireOp",EDGE,"E30.MirrorCS")])],"isStart":false});
            chamfer(context, id + "F7", {"entities" : qUnion([Q0, Q1]), "chamferType" : ChamferType.OFFSET_ANGLE, "width" : 7 * mm, "oppositeDirection" : true, "angle" : 20 * degree, "tangentPropagation" : true});
        }
        {
            var Q0;
            Q0=makeQuery(id+"F1.opExtrude","CAP_EDGE",EDGE,{"disambiguationData":[OSD([sQuery(id+"F0.wireOp",EDGE,"E32.MirrorCS")])],"isStart":true});
            var Q1;
            Q1=makeQuery(id+"F1.opExtrude","CAP_EDGE",EDGE,{"disambiguationData":[OSD([sQuery(id+"F0.wireOp",EDGE,"E32.MirrorCS")])],"isStart":false});
            var Q2;
            Q2=makeQuery(id+"F1.opExtrude","CAP_EDGE",EDGE,{"disambiguationData":[OSD([sQuery(id+"F0.wireOp",EDGE,"E29.MirrorCS")])],"isStart":false});
            var Q3;
            Q3=makeQuery(id+"F1.opExtrude","CAP_EDGE",EDGE,{"disambiguationData":[OSD([sQuery(id+"F0.wireOp",EDGE,"E29.MirrorCS")])],"isStart":true});
            var Q4;
            Q4=makeQuery(id+"F1.opExtrude","CAP_EDGE",EDGE,{"disambiguationData":[OSD([sQuery(id+"F0.wireOp",EDGE,"E10")])],"isStart":true});
            var Q5;
            Q5=makeQuery(id+"F1.opExtrude","CAP_EDGE",EDGE,{"disambiguationData":[OSD([sQuery(id+"F0.wireOp",EDGE,"E10")])],"isStart":false});
            var Q6;
            Q6=makeQuery(id+"F1.opExtrude","CAP_EDGE",EDGE,{"disambiguationData":[OSD([sQuery(id+"F0.wireOp",EDGE,"E15.MirrorCS")])],"isStart":false});
            var Q7;
            Q7=makeQuery(id+"F1.opExtrude","CAP_EDGE",EDGE,{"disambiguationData":[OSD([sQuery(id+"F0.wireOp",EDGE,"E15.MirrorCS")])],"isStart":true});
            chamfer(context, id + "F8", {"entities" : qUnion([Q0, Q1, Q2, Q3, Q4, Q5, Q6, Q7]), "width" : 2 * mm, "tangentPropagation" : true});
        }
    });
